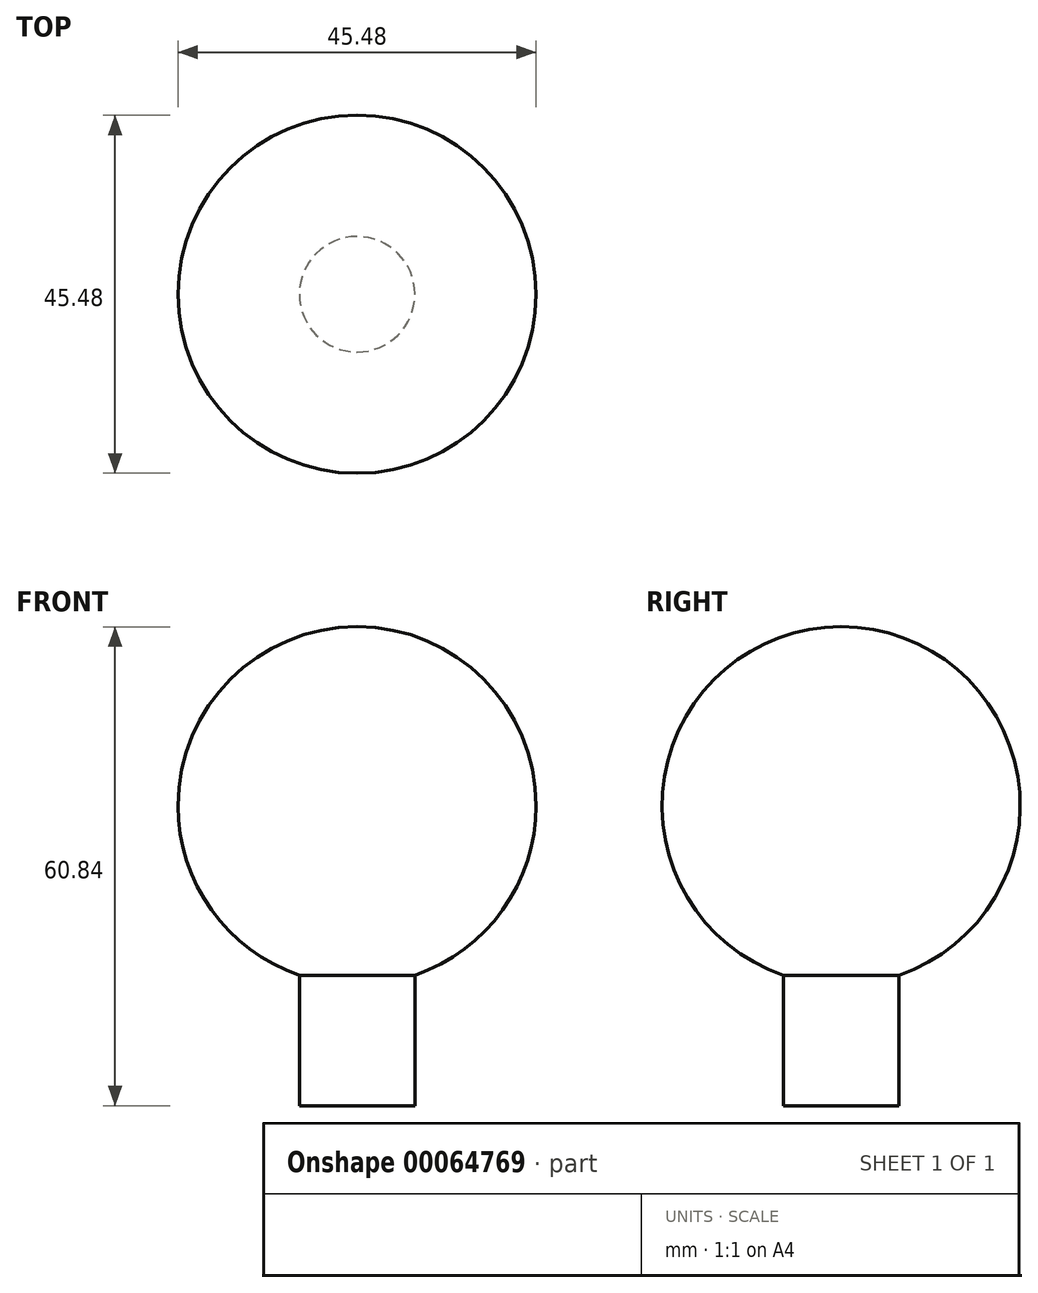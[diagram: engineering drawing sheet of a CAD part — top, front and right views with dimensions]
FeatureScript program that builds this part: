
annotation { "Feature Type Name" : "Feature", "Feature Type Description" : "" }
export const myFeature = defineFeature(function(context is Context, id is Id, definition is map)
    precondition{}
    {
        {
            var Q0;
            Q0=qCreatedBy(makeId("Front.planeOp"),FACE);
            var sketch = newSketch(context, id + "F0", { "sketchPlane" : qUnion([Q0])});
            skCircle(sketch, "E0", {"center": v(0, 0) * mm, "radius": 22.74 * mm});
            skLineSegment(sketch, "E1", {"start": v(-22.74, 0) * mm, "end": v(22.74, 0) * mm});
            skSolve(sketch);
        }
        {
            var Q0;
            {var subQ0=sQuery(id+"F0.wireOp",EDGE,"E1");Q0=makeQuery(id+"F0.imprint","IMPRINT",FACE,{"disambiguationData":[TD([[makeQuery(id+"F0.imprint","IMPRINT",EDGE,{"derivedFrom":subQ0}),-1.0]])]});}
            var Q1;
            Q1=sQuery(id+"F0.wireOp",EDGE,"E1");
            revolve(context, id + "F1", {"entities" : qUnion([Q0]), "axis" : qUnion([Q1]), "revolveType" : RevolveType.FULL});
        }
        {
            var Q0;
            Q0=qCreatedBy(makeId("Top.planeOp"),FACE);
            var sketch = newSketch(context, id + "F2", { "sketchPlane" : qUnion([Q0])});
            skCircle(sketch, "E2", {"center": v(0, 0) * mm, "radius": 7.33 * mm});
            skSolve(sketch);
        }
        {
            var Q0;
            Q0 = qSketchRegion(id + "F2", true);
            extrude(context, id + "F3", {"entities" : qUnion([Q0]), "operationType" : NewBodyOperationType.ADD, "oppositeDirection" : true, "depth" : 38.1 * mm});
        }
    });
